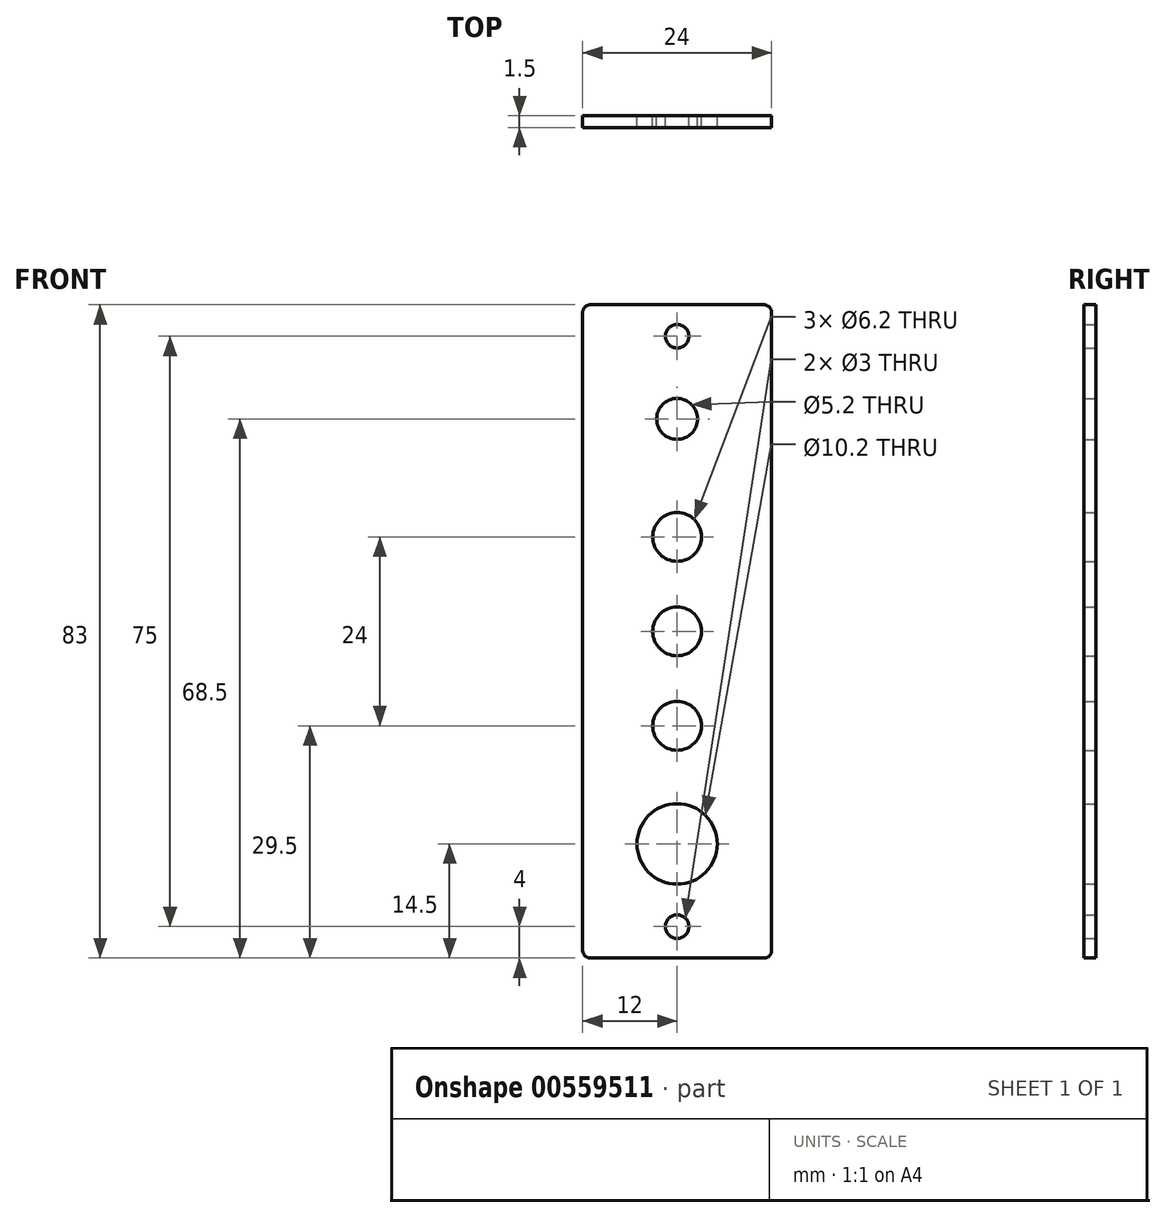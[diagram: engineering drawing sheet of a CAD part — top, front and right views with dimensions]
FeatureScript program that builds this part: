
annotation { "Feature Type Name" : "Feature", "Feature Type Description" : "" }
export const myFeature = defineFeature(function(context is Context, id is Id, definition is map)
    precondition{}
    {
        {
            var Q0;
            Q0=qCreatedBy(makeId("Front.planeOp"),FACE);
            var sketch = newSketch(context, id + "F0", { "sketchPlane" : qUnion([Q0])});
            skLineSegment(sketch, "E0.bottom", {"start": v(12, -41.5) * mm, "end": v(-12, -41.5) * mm});
            skLineSegment(sketch, "E0.top", {"start": v(12, 41.5) * mm, "end": v(-12, 41.5) * mm});
            skLineSegment(sketch, "E0.left", {"start": v(12, -41.5) * mm, "end": v(12, 41.5) * mm});
            skLineSegment(sketch, "E0.right", {"start": v(-12, -41.5) * mm, "end": v(-12, 41.5) * mm});
            skPoint(sketch, "E0.middle", {"position": v(0, 0) * mm});
            skCircle(sketch, "E1", {"center": v(0, 37.5) * mm, "radius": 1.5 * mm});
            skCircle(sketch, "E2", {"center": v(0, -37.5) * mm, "radius": 1.5 * mm});
            skCircle(sketch, "E3", {"center": v(0, 27) * mm, "radius": 2.6 * mm});
            skCircle(sketch, "E4", {"center": v(0, 12) * mm, "radius": 3.1 * mm});
            skCircle(sketch, "E5", {"center": v(0, 0) * mm, "radius": 3.1 * mm});
            skCircle(sketch, "E6", {"center": v(0, -12) * mm, "radius": 3.1 * mm});
            skCircle(sketch, "E7", {"center": v(0, -27) * mm, "radius": 5.1 * mm});
            skSolve(sketch);
        }
        {
            var Q0;
            Q0=qSketchRegion(id+"F0",true);
            extrude(context, id + "F1", {"entities" : qUnion([Q0]), "depth" : 1.5 * mm});
        }
        {
            var Q0;
            Q0=makeQuery(id+"F1.opExtrude","SWEPT_EDGE",EDGE,{"disambiguationData":[OSD([sQuery(id+"F0.wireOp",EDGE,"E0.top"),sQuery(id+"F0.wireOp",EDGE,"E0.right")])]});
            var Q1;
            Q1=makeQuery(id+"F1.opExtrude","SWEPT_EDGE",EDGE,{"disambiguationData":[OSD([sQuery(id+"F0.wireOp",EDGE,"E0.top"),sQuery(id+"F0.wireOp",EDGE,"E0.left")])]});
            var Q2;
            Q2=makeQuery(id+"F1.opExtrude","SWEPT_EDGE",EDGE,{"disambiguationData":[OSD([sQuery(id+"F0.wireOp",EDGE,"E0.bottom"),sQuery(id+"F0.wireOp",EDGE,"E0.left")])]});
            var Q3;
            Q3=makeQuery(id+"F1.opExtrude","SWEPT_EDGE",EDGE,{"disambiguationData":[OSD([sQuery(id+"F0.wireOp",EDGE,"E0.bottom"),sQuery(id+"F0.wireOp",EDGE,"E0.right")])]});
            fillet(context, id + "F2", {"entities" : qUnion([Q0, Q1, Q2, Q3]), "radius" : 1 * mm, "tangentPropagation" : true, "allowEdgeOverflow" : false});
        }
    });
